# Revit family: Seating-Teknion-NBAP_Banqs_Unthethered_Cushion-R2019
name_source: partatom
category: Furniture
units: mm (PartAtom-declared; Revit-internal decimal feet)

## family parameters
Always vertical = Yes
Cut with Voids When Loaded = No
OmniClass Number = 23.40.20.00
OmniClass Title = General Furniture and Specialties
Room Calculation Point = No
Shared = Yes
Work Plane-Based = No

## types (1)
- Soft-Seating Banqs Untethered Cushion
    Assembly Code = E2020200
    Description = Soft-Seating Banqs Untethered Cushion
    Manufacturer = Teknion
    Manufacturer Fax = 416.661.4586
    Model = NBAPR
    Part Number = NBAP
    Product Documentation Link = https://www.teknion.com
    Product Line = Banqs
    Product Page URL = https://www.teknion.com
    Series = Seating
    Sustainability Data = https://www.teknion.com
    URL = www.teknion.com
    Unit Weight URL = http://www.teknion.com
    Warranty = http://www.teknion.com

## geometry (parser evidence)
native form markers: Sweep x2
no freeform markers — native parametric forms only
